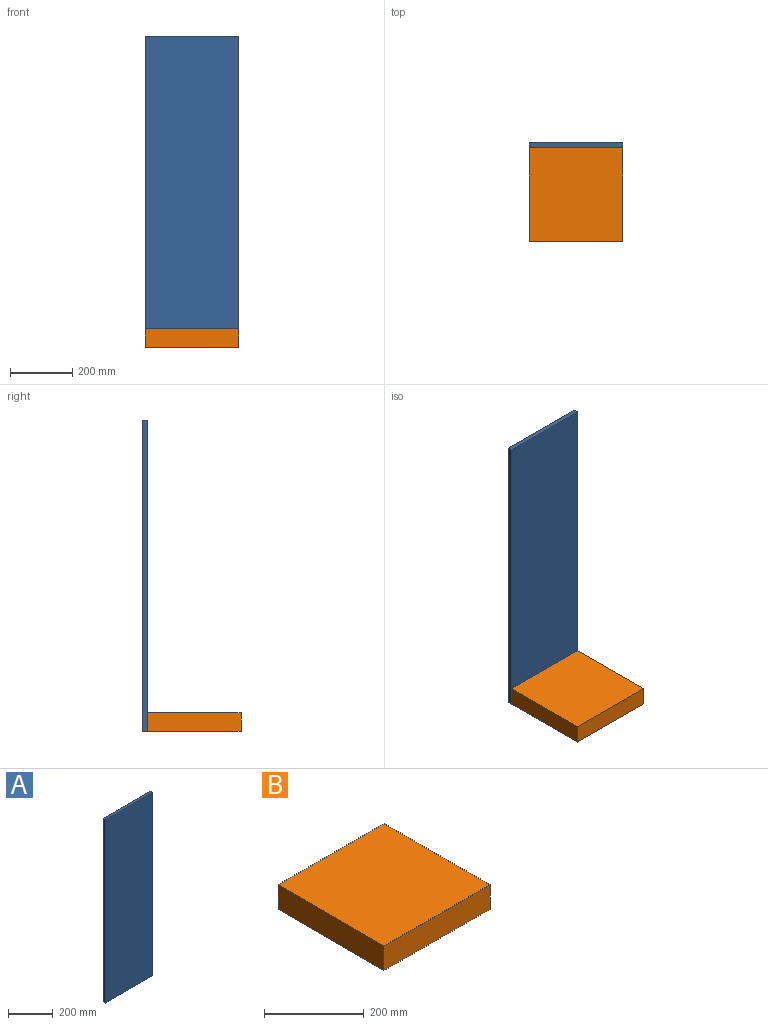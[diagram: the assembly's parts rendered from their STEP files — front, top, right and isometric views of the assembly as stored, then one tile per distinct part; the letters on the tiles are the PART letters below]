
ASSEMBLY  parts=2 mates=1
PART A: 6 faces, bbox 300x15x1000 mm
  f0: plane 300x15mm, normal (0,0,-1), area 4500mm2, adj f1,f3,f4,f5
  f1: plane 1000x15mm, normal (1,0,0), area 15000mm2, adj f0,f2,f4,f5
  f2: plane 300x15mm, normal (0,0,1), area 4500mm2, adj f1,f3,f4,f5
  f3: plane 1000x15mm, normal (-1,0,0), area 15000mm2, adj f0,f2,f4,f5
  f4: plane 1000x300mm, normal (0,-1,0), area 300000mm2, adj f0,f1,f2,f3
  f5: plane 1000x300mm, normal (0,1,0), area 300000mm2, adj f0,f1,f2,f3
PART B: 6 faces, bbox 300x300x60 mm
  f0: plane 300x300mm, normal (0,0,1), area 90000mm2, adj f1,f3,f4,f5
  f1: plane 300x60mm, normal (-1,0,0), area 18000mm2, adj f0,f2,f4,f5
  f2: plane 300x300mm, normal (0,0,-1), area 90000mm2, adj f1,f3,f4,f5
  f3: plane 300x60mm, normal (1,0,0), area 18000mm2, adj f0,f2,f4,f5
  f4: plane 300x60mm, normal (0,-1,0), area 18000mm2, adj f0,f1,f2,f3
  f5: plane 300x60mm, normal (0,1,0), area 18000mm2, adj f0,f1,f2,f3
PLACE A t=(31.55,1.27,37.37)mm
PLACE B t=(32.16,-13.73,-432.13)mm
MATE planar B.f5 <-> A.f4  axis (0,1,0) through (182.16,-13.73,-462.13)mm
